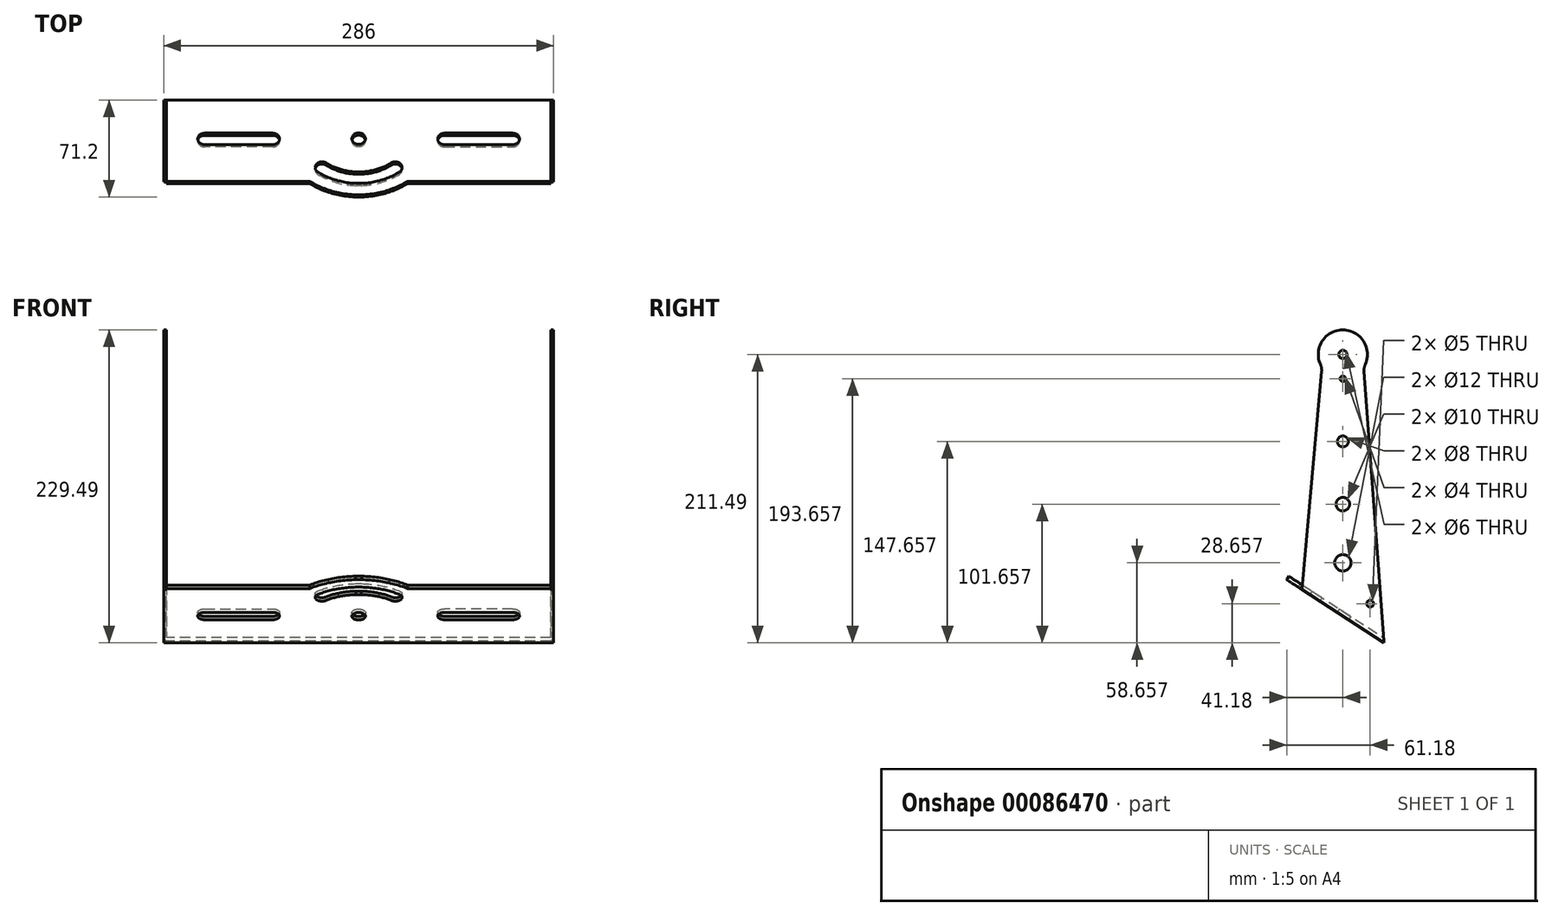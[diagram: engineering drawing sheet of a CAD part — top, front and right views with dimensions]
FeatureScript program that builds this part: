
annotation { "Feature Type Name" : "Feature", "Feature Type Description" : "" }
export const myFeature = defineFeature(function(context is Context, id is Id, definition is map)
    precondition{}
    {
        {
            var Q0;
            Q0=qCreatedBy(makeId("Front.planeOp"),FACE);
            var sketch = newSketch(context, id + "F0", { "sketchPlane" : qUnion([Q0])});
            skLineSegment(sketch, "E0.top", {"start": v(-143, 0) * mm, "end": v(143, 0) * mm});
            skLineSegment(sketch, "E0.left", {"start": v(-143, 230) * mm, "end": v(-143, 0) * mm});
            skLineSegment(sketch, "E0.right", {"start": v(143, 230) * mm, "end": v(143, 0) * mm});
            skLineSegment(sketch, "E1", {"start": v(0, -14.85) * mm, "end": v(0, 115.4) * mm, "construction": true});
            skLineSegment(sketch, "E2.0", {"start": v(141, 230) * mm, "end": v(141, 2) * mm});
            skLineSegment(sketch, "E2.1", {"start": v(-141, 2) * mm, "end": v(141, 2) * mm});
            skLineSegment(sketch, "E2.2", {"start": v(-141, 230) * mm, "end": v(-141, 2) * mm});
            skLineSegment(sketch, "E3", {"start": v(-143, 230) * mm, "end": v(-141, 230) * mm});
            skLineSegment(sketch, "E4", {"start": v(143, 230) * mm, "end": v(141, 230) * mm});
            skSolve(sketch);
        }
        {
            var Q0;
            Q0=qSketchRegion(id+"F0",true);
            extrude(context, id + "F1", {"entities" : qUnion([Q0]), "endBound" : BoundingType.SYMMETRIC, "depth" : 60 * mm});
        }
        {
            var Q0;
            Q0=qCreatedBy(makeId("Right.planeOp"),FACE);
            var sketch = newSketch(context, id + "F2", { "sketchPlane" : qUnion([Q0])});
            skLineSegment(sketch, "E5", {"start": v(30.06, 20) * mm, "end": v(-30.02, 20) * mm, "construction": true});
            skLineSegment(sketch, "E6", {"start": v(0, 0) * mm, "end": v(0.02, 60) * mm, "construction": true});
            skPoint(sketch, "E6.endSnap0", {"position": v(0.02, 20) * mm});
            skSolve(sketch);
        }
        {
            var Q0;
            Q0=qCreatedBy(makeId("Front.planeOp"),FACE);
            var sketch = newSketch(context, id + "F3", { "sketchPlane" : qUnion([Q0])});
            skLineSegment(sketch, "E7", {"start": v(-140.41, 20) * mm, "end": v(139.83, 20) * mm, "construction": true});
            skSolve(sketch);
        }
        {
            var Q0;
            Q0=sQuery(id+"F3.wireOp",EDGE,"E7");
            cPlane(context, id + "F4", {"entities" : qUnion([Q0]), "cplaneType" : CPlaneType.LINE_ANGLE, "offset" : 150 * mm, "angle" : 57 * degree, "width" : 150 * mm, "height" : 150 * mm});
        }
        {
            var Q0;
            Q0=qCreatedBy(id+"F4.planeOp",FACE);
            var sketch = newSketch(context, id + "F5", { "sketchPlane" : qUnion([Q0])});
            skLineSegment(sketch, "E8.bottom", {"start": v(141, -60) * mm, "end": v(-141, -60) * mm});
            skLineSegment(sketch, "E8.top", {"start": v(141, 60) * mm, "end": v(-141, 60) * mm});
            skLineSegment(sketch, "E8.left", {"start": v(141, -60) * mm, "end": v(141, 60) * mm});
            skLineSegment(sketch, "E8.right", {"start": v(-141, -60) * mm, "end": v(-141, 60) * mm});
            skPoint(sketch, "E8.middle", {"position": v(0, 0) * mm});
            skSolve(sketch);
        }
        {
            var Q0;
            Q0=qSketchRegion(id+"F5",true);
            extrude(context, id + "F6", {"entities" : qUnion([Q0]), "operationType" : NewBodyOperationType.ADD, "depth" : 3 * mm});
        }
        {
            var Q0;
            Q0=qCreatedBy(makeId("Right.planeOp"),FACE);
            var sketch = newSketch(context, id + "F7", { "sketchPlane" : qUnion([Q0])});
            skLineSegment(sketch, "E9.bottom", {"start": v(30.02, 6.7) * mm, "end": v(73.8, 6.7) * mm});
            skLineSegment(sketch, "E9.top", {"start": v(30.02, -22.13) * mm, "end": v(73.8, -22.13) * mm});
            skLineSegment(sketch, "E9.left", {"start": v(30.02, 6.7) * mm, "end": v(30.02, -22.13) * mm});
            skLineSegment(sketch, "E9.right", {"start": v(73.8, 6.7) * mm, "end": v(73.8, -22.13) * mm});
            skSolve(sketch);
        }
        {
            var Q0;
            Q0=qSketchRegion(id+"F7",true);
            extrude(context, id + "F8", {"entities" : qUnion([Q0]), "operationType" : NewBodyOperationType.REMOVE, "endBound" : BoundingType.SYMMETRIC, "oppositeDirection" : true, "depth" : 400 * mm});
        }
        {
            var Q0;
            Q0=qCreatedBy(id+"F4.planeOp",FACE);
            var sketch = newSketch(context, id + "F9", { "sketchPlane" : qUnion([Q0])});
            skLineSegment(sketch, "E10.bottom", {"start": v(-213.33, -151.27) * mm, "end": v(213.33, -151.27) * mm});
            skLineSegment(sketch, "E10.top", {"start": v(-213.33, 151.27) * mm, "end": v(213.33, 151.27) * mm});
            skLineSegment(sketch, "E10.left", {"start": v(-213.33, -151.27) * mm, "end": v(-213.33, 151.27) * mm});
            skLineSegment(sketch, "E10.right", {"start": v(213.33, -151.27) * mm, "end": v(213.33, 151.27) * mm});
            skPoint(sketch, "E10.middle", {"position": v(0, 0) * mm});
            skSolve(sketch);
        }
        {
            var Q0;
            Q0=qSketchRegion(id+"F9",true);
            extrude(context, id + "F10", {"entities" : qUnion([Q0]), "operationType" : NewBodyOperationType.REMOVE, "oppositeDirection" : true, "depth" : 178.84 * mm});
        }
        {
            var Q0;
            Q0=qCreatedBy(id+"F4.planeOp",FACE);
            var sketch = newSketch(context, id + "F11", { "sketchPlane" : qUnion([Q0])});
            skLineSegment(sketch, "E11", {"start": v(-141, -39.83) * mm, "end": v(170.93, -39.83) * mm, "construction": true});
            skLineSegment(sketch, "E12", {"start": v(-147.2, -48.15) * mm, "end": v(-35.87, -48.15) * mm});
            skArc(sketch, "E13", {"start": v(-35.87, -48.15) * mm, "mid": v(0, -60.04) * mm, "end": v(35.87, -48.15) * mm});
            skLineSegment(sketch, "E14", {"start": v(146.36, -48.15) * mm, "end": v(146.36, -83.3) * mm});
            skLineSegment(sketch, "E15", {"start": v(146.36, -83.3) * mm, "end": v(-147.2, -83.3) * mm});
            skLineSegment(sketch, "E16", {"start": v(-147.2, -83.3) * mm, "end": v(-147.2, -48.15) * mm});
            skLineSegment(sketch, "E17.trimOffspring", {"start": v(35.87, -48.15) * mm, "end": v(146.36, -48.15) * mm});
            skSolve(sketch);
        }
        {
            var Q0;
            Q0=qSketchRegion(id+"F11",true);
            extrude(context, id + "F12", {"entities" : qUnion([Q0]), "operationType" : NewBodyOperationType.REMOVE, "depth" : 3.8 * mm});
        }
        {
            var Q0;
            Q0=qCreatedBy(id+"F4.planeOp",FACE);
            var sketch = newSketch(context, id + "F13", { "sketchPlane" : qUnion([Q0])});
            skCircle(sketch, "E18", {"center": v(0, -10.88) * mm, "radius": 5 * mm});
            skArc(sketch, "E19.0", {"start": v(2, -45) * mm, "mid": v(15.13, -42.43) * mm, "end": v(26.91, -36.12) * mm});
            skLineSegment(sketch, "E19.1", {"start": v(2, -45) * mm, "end": v(-2, -45) * mm});
            skArc(sketch, "E19.2", {"start": v(-26.91, -36.12) * mm, "mid": v(-15.13, -42.43) * mm, "end": v(-2, -45) * mm});
            skLineSegment(sketch, "E20", {"start": v(63, -11.1) * mm, "end": v(113, -11.1) * mm});
            skLineSegment(sketch, "E21.MirrorCS", {"start": v(-63, -11.1) * mm, "end": v(-113, -11.1) * mm});
            skArc(sketch, "E22.0.startCap", {"start": v(63, -16.1) * mm, "mid": v(58, -11.1) * mm, "end": v(63, -6.1) * mm});
            skArc(sketch, "E22.0.endCap", {"start": v(113, -6.1) * mm, "mid": v(118, -11.1) * mm, "end": v(113, -16.1) * mm});
            skLineSegment(sketch, "E22.0.left", {"start": v(63, -6.1) * mm, "end": v(113, -6.1) * mm});
            skLineSegment(sketch, "E22.0.right", {"start": v(63, -16.1) * mm, "end": v(113, -16.1) * mm});
            skArc(sketch, "E23.0.startCap", {"start": v(2.23, -50) * mm, "mid": v(-2.99, -45.22) * mm, "end": v(1.78, -40) * mm});
            skArc(sketch, "E23.0.endCap", {"start": v(23.92, -32.11) * mm, "mid": v(30.92, -33.13) * mm, "end": v(29.9, -40.13) * mm});
            skArc(sketch, "E23.0.left", {"start": v(1.78, -40) * mm, "mid": v(13.45, -37.72) * mm, "end": v(23.92, -32.11) * mm});
            skArc(sketch, "E23.0.right", {"start": v(2.23, -50) * mm, "mid": v(16.8, -47.14) * mm, "end": v(29.9, -40.13) * mm});
            skArc(sketch, "E23.1.startCap", {"start": v(2, -40) * mm, "mid": v(7, -45) * mm, "end": v(2, -50) * mm});
            skArc(sketch, "E23.1.endCap", {"start": v(-2, -50) * mm, "mid": v(-7, -45) * mm, "end": v(-2, -40) * mm});
            skLineSegment(sketch, "E23.1.left", {"start": v(2, -50) * mm, "end": v(-2, -50) * mm});
            skLineSegment(sketch, "E23.1.right", {"start": v(2, -40) * mm, "end": v(-2, -40) * mm});
            skArc(sketch, "E23.2.startCap", {"start": v(-29.9, -40.13) * mm, "mid": v(-30.92, -33.13) * mm, "end": v(-23.92, -32.11) * mm});
            skArc(sketch, "E23.2.endCap", {"start": v(-1.78, -40) * mm, "mid": v(2.99, -45.22) * mm, "end": v(-2.23, -50) * mm});
            skArc(sketch, "E23.2.left", {"start": v(-23.92, -32.11) * mm, "mid": v(-13.45, -37.72) * mm, "end": v(-1.78, -40) * mm});
            skArc(sketch, "E23.2.right", {"start": v(-29.9, -40.13) * mm, "mid": v(-16.8, -47.14) * mm, "end": v(-2.23, -50) * mm});
            skArc(sketch, "E23.3.startCap", {"start": v(-63, -6.1) * mm, "mid": v(-58, -11.1) * mm, "end": v(-63, -16.1) * mm});
            skArc(sketch, "E23.3.endCap", {"start": v(-113, -16.1) * mm, "mid": v(-118, -11.1) * mm, "end": v(-113, -6.1) * mm});
            skLineSegment(sketch, "E23.3.left", {"start": v(-63, -16.1) * mm, "end": v(-113, -16.1) * mm});
            skLineSegment(sketch, "E23.3.right", {"start": v(-63, -6.1) * mm, "end": v(-113, -6.1) * mm});
            skSolve(sketch);
        }
        {
            var Q0;
            Q0=qSketchRegion(id+"F13",true);
            var Q1;
            {var subQ1=sQuery(id+"F13.wireOp",EDGE,"E19.1");Q1=makeQuery(id+"F13.imprint","IMPRINT",FACE,{"disambiguationData":[TD([[makeQuery(id+"F13.imprint","IMPRINT",EDGE,{"derivedFrom":subQ1}),-1.0]])]});}
            var Q2;
            {var subQ1=sQuery(id+"F13.wireOp",EDGE,"E19.1");Q2=makeQuery(id+"F13.imprint","IMPRINT",FACE,{"disambiguationData":[TD([[makeQuery(id+"F13.imprint","IMPRINT",EDGE,{"derivedFrom":subQ1}),1.0]])]});}
            extrude(context, id + "F14", {"entities" : qUnion([Q0, Q1, Q2]), "operationType" : NewBodyOperationType.REMOVE, "depth" : 5.04 * mm});
        }
        {
            var Q0;
            Q0=qCreatedBy(makeId("Right.planeOp"),FACE);
            var sketch = newSketch(context, id + "F15", { "sketchPlane" : qUnion([Q0])});
            skArc(sketch, "E24", {"start": v(16.44, 204.67) * mm, "mid": v(-0.08, 230) * mm, "end": v(-16.38, 204.53) * mm});
            skLineSegment(sketch, "E25", {"start": v(-29.6, 43.48) * mm, "end": v(-15.52, 199.48) * mm});
            skPoint(sketch, "E26.visualSharp", {"position": v(-15.25, 202.44) * mm});
            skArc(sketch, "E26.filletArc", {"start": v(-15.52, 199.48) * mm, "mid": v(-15.62, 202.06) * mm, "end": v(-16.38, 204.53) * mm});
            skPoint(sketch, "E27.visualSharp", {"position": v(15.35, 202.6) * mm});
            skArc(sketch, "E27.filletArc", {"start": v(16.44, 204.67) * mm, "mid": v(15.7, 202.24) * mm, "end": v(15.61, 199.7) * mm});
            skLineSegment(sketch, "E28", {"start": v(-29.6, 43.48) * mm, "end": v(-42.37, 52.13) * mm});
            skLineSegment(sketch, "E29", {"start": v(-42.37, 52.13) * mm, "end": v(-42.37, 273.47) * mm});
            skLineSegment(sketch, "E30", {"start": v(-42.37, 273.47) * mm, "end": v(77.63, 273.47) * mm});
            skLineSegment(sketch, "E31", {"start": v(77.63, 273.47) * mm, "end": v(77.63, 43.47) * mm});
            skLineSegment(sketch, "E32", {"start": v(30.15, 0) * mm, "end": v(15.61, 199.7) * mm});
            skLineSegment(sketch, "E33", {"start": v(30.15, 0) * mm, "end": v(77.63, 0) * mm});
            skLineSegment(sketch, "E34", {"start": v(77.63, 0) * mm, "end": v(77.63, 43.47) * mm});
            skSolve(sketch);
        }
        {
            var Q0;
            Q0=qSketchRegion(id+"F15",true);
            extrude(context, id + "F16", {"entities" : qUnion([Q0]), "operationType" : NewBodyOperationType.REMOVE, "endBound" : BoundingType.SYMMETRIC, "oppositeDirection" : true, "depth" : 500 * mm});
        }
        {
            var Q0;
            Q0=qCreatedBy(makeId("Right.planeOp"),FACE);
            var sketch = newSketch(context, id + "F17", { "sketchPlane" : qUnion([Q0])});
            skCircle(sketch, "E35", {"center": v(0, 212) * mm, "radius": 3 * mm});
            skCircle(sketch, "E36", {"center": v(0, 194.17) * mm, "radius": 2 * mm});
            skCircle(sketch, "E37", {"center": v(0, 148.17) * mm, "radius": 4 * mm});
            skCircle(sketch, "E38", {"center": v(0, 102.17) * mm, "radius": 5 * mm});
            skCircle(sketch, "E39", {"center": v(0, 59.17) * mm, "radius": 6 * mm});
            skCircle(sketch, "E40", {"center": v(20, 29.17) * mm, "radius": 2.5 * mm});
            skSolve(sketch);
        }
        {
            var Q0;
            Q0=qSketchRegion(id+"F17",true);
            extrude(context, id + "F18", {"entities" : qUnion([Q0]), "operationType" : NewBodyOperationType.REMOVE, "endBound" : BoundingType.SYMMETRIC, "oppositeDirection" : true, "depth" : 320 * mm});
        }
    });
